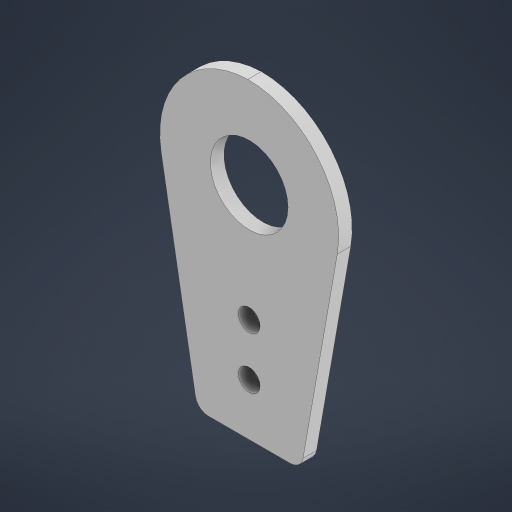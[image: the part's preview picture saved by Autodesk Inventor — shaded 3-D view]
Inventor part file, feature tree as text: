
AUTODESK INVENTOR PART (.ipt)
format: ipt  version: 2024 (Build 280153000, 153)  size: 214,528 bytes
history: native  units: in
note: dims shown in document units (in); Inventor stores cm internally (conversion verified against a paired STEP export)
features: fillet x6, extrude x1, sketch x1
ambient origin geometry x8: Origin, YZ Plane, XZ Plane, XY Plane, X Axis, Y Axis, Z Axis, Center Point
bodies: Solid1 (feature_tree)
feature tree (8):
  extrude  "Extrusion1"  Depth=0.125in
  fillet  "Fillet9"  Radius=0.209in
  fillet  "Fillet10"  Radius=0.209in
  fillet  "Fillet11"  Radius=0.875in
  fillet  "Fillet12"  Radius=2.0in
  fillet  "Fillet13"  Radius=2.5in
  fillet  "Fillet14"  Radius=0.875in
  sketch  "Sketch1"  dims[d0=1.75in d2=0.748in d3=0.209in d4=0.209in d5=0.875in d6=2.0in d7=2.5in d8=0.875in d9=0.875in d10=0.13in d11=0.0in d20=0.5in d21=0.5in d22=0.875in d23=0.875in d24=0.125in d25=0.125in d16=0.0in d17=0.0in d18=0.0in d19=0.0in]
